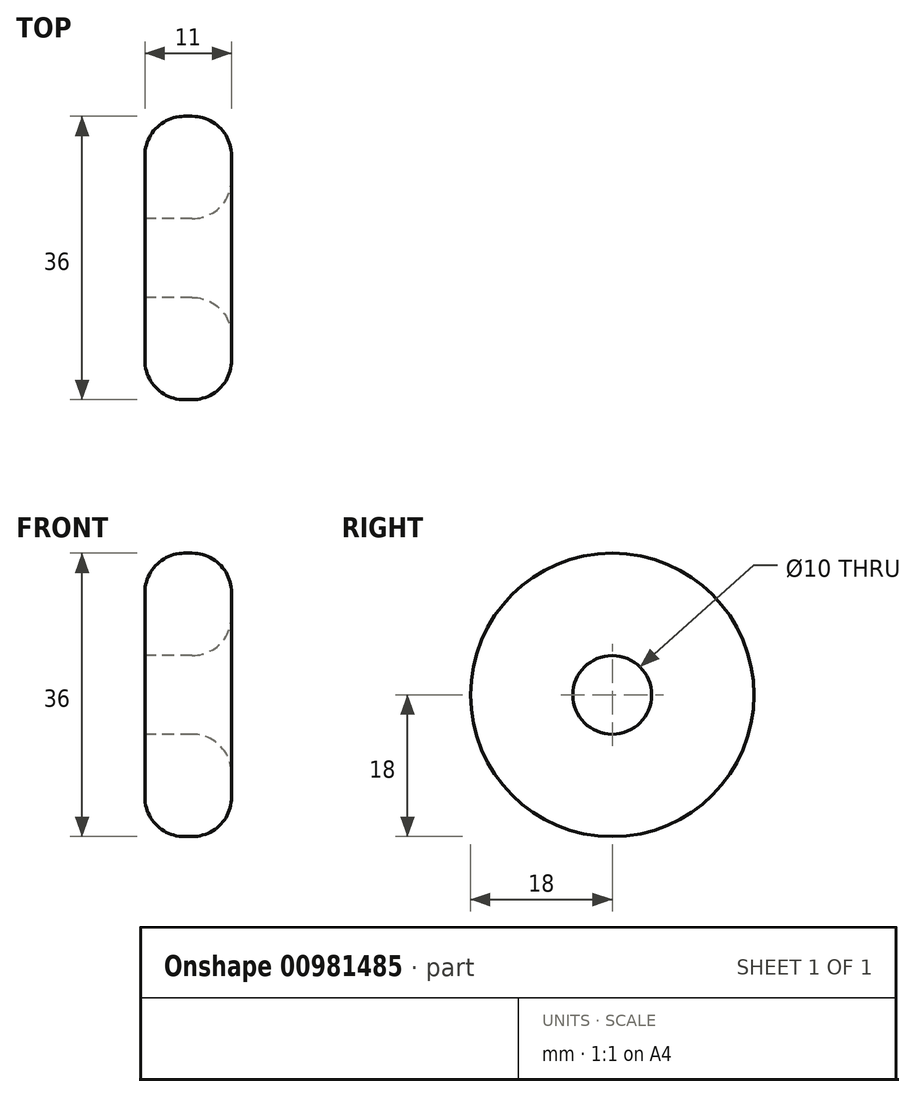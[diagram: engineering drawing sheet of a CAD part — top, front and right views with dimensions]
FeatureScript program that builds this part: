
annotation { "Feature Type Name" : "Feature", "Feature Type Description" : "" }
export const myFeature = defineFeature(function(context is Context, id is Id, definition is map)
    precondition{}
    {
        {
            var Q0;
            Q0=qCreatedBy(makeId("Right.planeOp"),FACE);
            var sketch = newSketch(context, id + "F0", { "sketchPlane" : qUnion([Q0])});
            skCircle(sketch, "E0", {"center": v(0, 0) * mm, "radius": 18 * mm});
            skCircle(sketch, "E1", {"center": v(0, 0) * mm, "radius": 5 * mm});
            skSolve(sketch);
        }
        {
            var Q0;
            Q0=makeQuery(id+"F0.imprint","IMPRINT",FACE,{"disambiguationData":[TD([[makeQuery(id+"F0.imprint","IMPRINT",EDGE,{"derivedFrom":sQuery(id+"F0.wireOp",EDGE,"E0")}),1.0]])]});
            extrude(context, id + "F1", {"entities" : qUnion([Q0]), "depth" : 11 * mm, "offsetDistance" : 25 * mm});
        }
        {
            var Q0;
            Q0=makeQuery(id+"F1.opExtrude","SWEPT_FACE",FACE,{"disambiguationData":[OSD([sQuery(id+"F0.wireOp",EDGE,"E0")])]});
            var Q1;
            Q1=makeQuery(id+"F1.opExtrude","CAP_FACE",FACE,{"disambiguationData":[OSD([sQuery(id+"F0.wireOp",EDGE,"E0")])],"isStart":false});
            fillet(context, id + "F2", {"entities" : qUnion([Q0, Q1]), "radius" : 5 * mm, "tangentPropagation" : true, "allowEdgeOverflow" : false});
        }
    });
